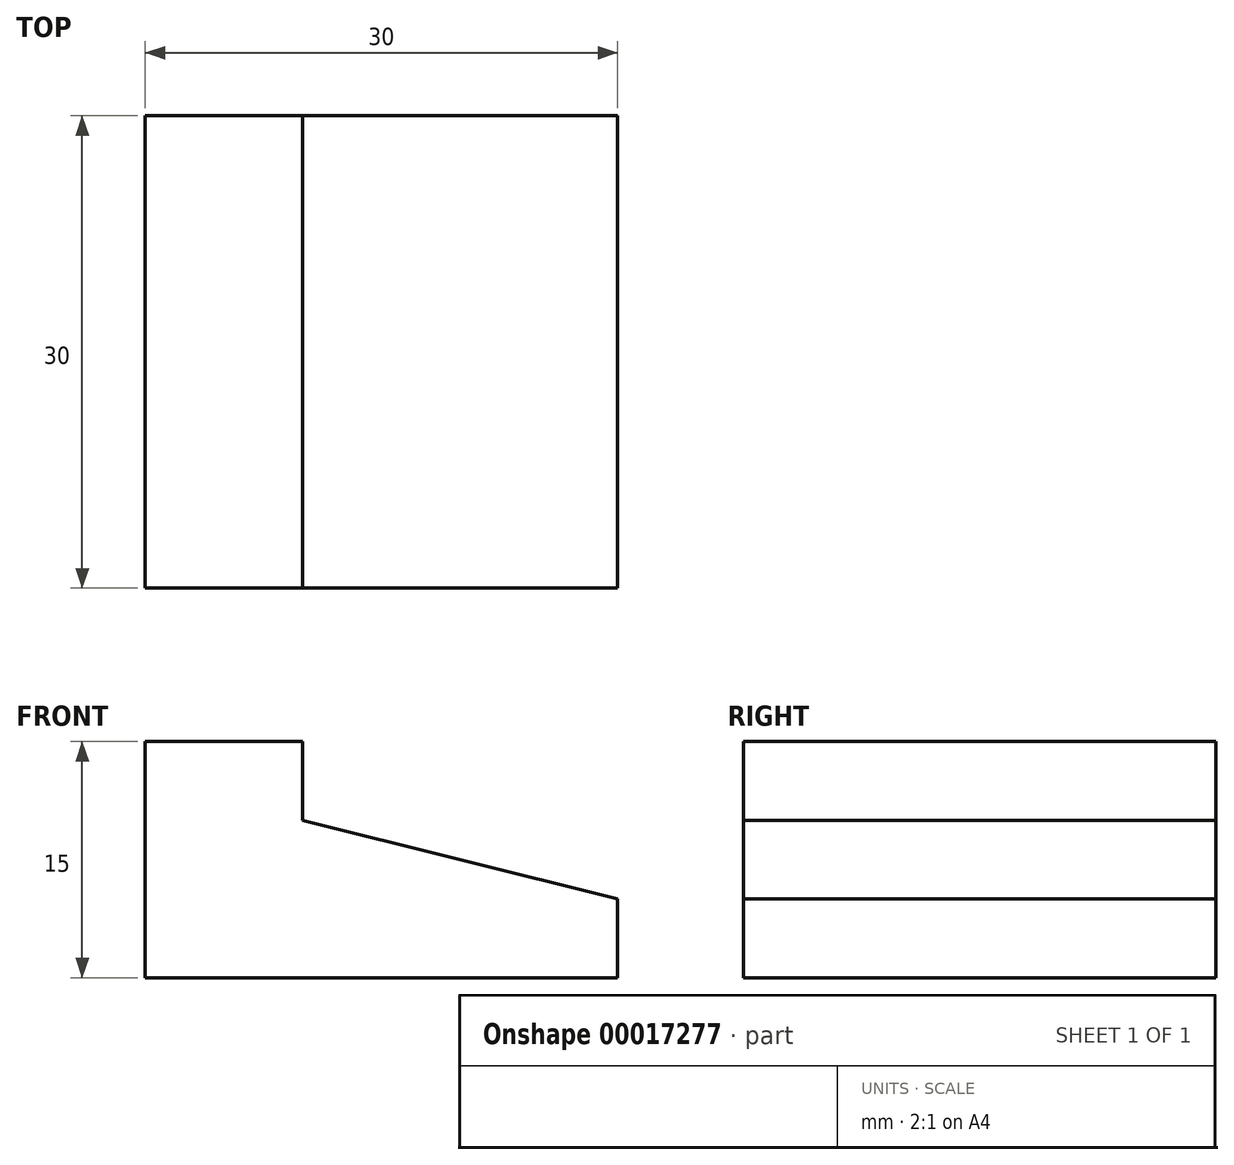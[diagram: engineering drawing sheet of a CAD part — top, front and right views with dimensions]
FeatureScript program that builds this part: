
annotation { "Feature Type Name" : "Feature", "Feature Type Description" : "" }
export const myFeature = defineFeature(function(context is Context, id is Id, definition is map)
    precondition{}
    {
        {
            var Q0;
            Q0=qCreatedBy(makeId("Front.planeOp"),FACE);
            var sketch = newSketch(context, id + "F0", { "sketchPlane" : qUnion([Q0])});
            skLineSegment(sketch, "E0", {"start": v(-47.64, -3.12) * mm, "end": v(-47.64, 11.88) * mm});
            skLineSegment(sketch, "E1", {"start": v(-17.64, -3.12) * mm, "end": v(-47.64, -3.12) * mm});
            skLineSegment(sketch, "E2", {"start": v(-17.64, -3.12) * mm, "end": v(-17.64, 1.88) * mm});
            skLineSegment(sketch, "E3", {"start": v(-47.64, 11.88) * mm, "end": v(-37.64, 11.88) * mm});
            skLineSegment(sketch, "E4", {"start": v(-37.64, 11.88) * mm, "end": v(-37.64, 6.88) * mm});
            skLineSegment(sketch, "E5", {"start": v(-37.64, 6.88) * mm, "end": v(-17.64, 1.88) * mm});
            skSolve(sketch);
        }
        {
            var Q0;
            Q0=makeQuery(id+"F0.imprint","IMPRINT",FACE,{"disambiguationData":[TD([[makeQuery(id+"F0.imprint","IMPRINT",EDGE,{"derivedFrom":sQuery(id+"F0.wireOp",EDGE,"E0")}),-1.0]])]});
            extrude(context, id + "F1", {"entities" : qUnion([Q0]), "depth" : 30 * mm});
        }
    });
